# Revit family: LAMP_OCULT SUSPENDED PROFILE
name_source: partatom
category: Luminarias
revit_build: Autodesk Revit 2015 (Build: 20140606_1530(x64)
units: mm (PartAtom-declared; Revit-internal decimal feet)

## types (32) — shared parameters
Comentarios de tipo = Availability of changing profile version and height when placed in project.
Elevación por defecto = 1219 mm
Fabricante = LAMP
IEE = A+
Installation instructions = https://www.lamp.es
Insulation class = I
Last update = 25/07/2019
Luminaire type = Profile
Manufacturer URL = http://www.lamp.es
Manufacturer country = Spain
Manufacturer name = LAMP
Material suspension = Panel de metal
Model explanation = Availability of changing profile version and height when placed in project.
Product URL = https://www.lamp.es
Product datasheet = http://www.lamp.es
Protection rating = IP20

## per-type parameters (varying)
| type | Descripción | Dimensions | Finish | Length | Material perfil | Modelo | Product code | Weight |
| 500mm Surface  BLACK | OCULT SYS. ACC. SUR PROFILE 500 BK. | 500x53x96 | Matte black RAL 9011 | 500 mm  [stored 1.64042 ft] | LAMP_Aluminio Ocult Pendular NG | OSSUPR500B | OSSUPR500B | 0.84 kg |
| 500mm Surface  WHITE | OCULT SYS. ACC. SUR PROFILE 500 WH. | 500x53x96 | Matte white RAL 9010 | 500 mm  [stored 1.64042 ft] | LAMP_Aluminio Ocult Pendular BL | OSSUPR500W | OSSUPR500W | 0.84 kg |
| 600mm Surface  BLACK | OCULT SYS. ACC. SUR PROFILE 600 BK. | 600x53x96 | Matte black RAL 9011 | 600 mm | LAMP_Aluminio Ocult Pendular NG | OSSUPR600B | OSSUPR600B | 1.03 kg |
| 600mm Surface  WHITE | OCULT SYS. ACC. SUR PROFILE 600 WH. | 600x53x96 | Matte white RAL 9010 | 600 mm | LAMP_Aluminio Ocult Pendular BL | OSSUPR600W | OSSUPR600W | 1.03 kg |
| 700mm Surface  BLACK | OCULT SYS. ACC. SUR PROFILE 700 BK. | 700x53x96 | Matte black RAL 9011 | 700 mm  [stored 2.29659 ft] | LAMP_Aluminio Ocult Pendular NG | OSSUPR700B | OSSUPR700B | 1.35 kg |
| 700mm Surface  WHITE | OCULT SYS. ACC. SUR PROFILE 700 WH. | 700x53x96 | Matte white RAL 9010 | 700 mm  [stored 2.29659 ft] | LAMP_Aluminio Ocult Pendular BL | OSSUPR700W | OSSUPR700W | 1.35 kg |
| 800mm Surface  BLACK | OCULT SYS. ACC. SUR PROFILE 800 BK. | 800x53x96 | Matte black RAL 9011 | 800 mm  [stored 2.62467 ft] | LAMP_Aluminio Ocult Pendular NG | OSSUPR800B | OSSUPR800B | 1.53 kg |
| 800mm Surface  WHITE | OCULT SYS. ACC. SUR PROFILE 800 WH. | 800x53x96 | Matte white RAL 9010 | 800 mm  [stored 2.62467 ft] | LAMP_Aluminio Ocult Pendular BL | OSSUPR800W | OSSUPR800W | 1.53 kg |
| 900mm Surface  BLACK | OCULT SYS. ACC. SUR PROFILE 900 BK. | 900x53x96 | Matte black RAL 9011 | 900 mm  [stored 2.95276 ft] | LAMP_Aluminio Ocult Pendular NG | OSSUPR900B | OSSUPR900B | 1.72 kg |
| 900mm Surface  WHITE | OCULT SYS. ACC. SUR PROFILE 900 WH. | 900x53x96 | Matte white RAL 9010 | 900 mm  [stored 2.95276 ft] | LAMP_Aluminio Ocult Pendular BL | OSSUPR900W | OSSUPR900W | 1.72 kg |
| 1000mm Surface  BLACK | OCULT SYS. ACC. SUR PROFILE 1000 BK. | 1000x53x96 | Matte black RAL 9011 | 1000 mm  [stored 3.28084 ft] | LAMP_Aluminio Ocult Pendular NG | OSSUPR1000B | OSSUPR1000B | 1.91 kg |
| 1000mm Surface  WHITE | OCULT SYS. ACC. SUR PROFILE 1000 WH. | 1000x53x96 | Matte white RAL 9010 | 1000 mm  [stored 3.28084 ft] | LAMP_Aluminio Ocult Pendular BL | OSSUPR1000W | OSSUPR1000W | 1.91 kg |
| 1100mm Surface  BLACK | OCULT SYS. ACC. SUR PROFILE 1100 BK. | 1100x53x96 | Matte black RAL 9011 | 1100 mm | LAMP_Aluminio Ocult Pendular NG | OSSUPR1100B | OSSUPR1100B | 2.10 kg |
| 1100mm Surface  WHITE | OCULT SYS. ACC. SUR PROFILE 1100 WH. | 1100x53x96 | Matte white RAL 9010 | 1100 mm | LAMP_Aluminio Ocult Pendular BL | OSSUPR1100W | OSSUPR1100W | 2.10 kg |
| 1200mm Surface  BLACK | OCULT SYS. ACC. SUR PROFILE 1200 BK. | 1200x53x96 | Matte black RAL 9011 | 1200 mm | LAMP_Aluminio Ocult Pendular NG | OSSUPR1200B | OSSUPR1200B | 2.42 kg |
| 1200mm Surface  WHITE | OCULT SYS. ACC. SUR PROFILE 1200 WH. | 1200x53x96 | Matte white RAL 9010 | 1200 mm | LAMP_Aluminio Ocult Pendular BL | OSSUPR1200W | OSSUPR1200W | 2.42 kg |
| 1300mm Surface  BLACK | OCULT SYS. ACC. SUR PROFILE 1300 BK. | 1300x53x96 | Matte black RAL 9011 | 1300 mm  [stored 4.26509 ft] | LAMP_Aluminio Ocult Pendular NG | OSSUPR1300B | OSSUPR1300B | 2.61 kg |
| 1300mm Surface  WHITE | OCULT SYS. ACC. SUR PROFILE 1300 WH | 1300x53x96 | Matte white RAL 9010 | 1300 mm  [stored 4.26509 ft] | LAMP_Aluminio Ocult Pendular BL | OSSUPR1300W | OSSUPR1300W | 2.61 kg |
| 1400mm Surface  BLACK | OCULT SYS. ACC. SUR PROFILE 1400 BK. | 1400x53x96 | Matte black RAL 9011 | 1400 mm  [stored 4.59318 ft] | LAMP_Aluminio Ocult Pendular NG | OSSUPR1400B | OSSUPR1400B | 2.79 kg |
| 1400mm Surface  WHITE | OCULT SYS. ACC. SUR PROFILE 1400 WH. | 1400x53x96 | Matte white RAL 9010 | 1400 mm  [stored 4.59318 ft] | LAMP_Aluminio Ocult Pendular BL | OSSUPR1400W | OSSUPR1400W | 2.79 kg |
| 1500mm Surface  BLACK | OCULT SYS. ACC. SUR PROFILE 1500 BK. | 1500x53x96 | Matte black RAL 9011 | 1500 mm  [stored 4.92126 ft] | LAMP_Aluminio Ocult Pendular NG | OSSUPR1500B | OSSUPR1500B | 2.98 kg |
| 1500mm Surface  WHITE | OCULT SYS. ACC. SUR PROFILE 1500 WH. | 1500x53x96 | Matte white RAL 9010 | 1500 mm  [stored 4.92126 ft] | LAMP_Aluminio Ocult Pendular BL | OSSUPR1500W | OSSUPR1500W | 2.98 kg |
| 1600mm Surface  BLACK | OCULT SYS. ACC. SUR PROFILE 1600 BK. | 1600x53x96 | Matte black RAL 9011 | 1600 mm  [stored 5.24934 ft] | LAMP_Aluminio Ocult Pendular NG | OSSUPR1600B | OSSUPR1600B | 3.17 kg |
| 1600mm Surface  WHITE | OCULT SYS. ACC. SUR PROFILE 1600 WH. | 1600x53x96 | Matte white RAL 9010 | 1600 mm  [stored 5.24934 ft] | LAMP_Aluminio Ocult Pendular BL | OSSUPR1600W | OSSUPR1600W | 3.17 kg |
| 1700mm Surface  BLACK | OCULT SYS. ACC. SUR PROFILE 1700 BK. | 1700x53x96 | Matte black RAL 9011 | 1700 mm  [stored 5.57743 ft] | LAMP_Aluminio Ocult Pendular NG | OSSUPR1700B | OSSUPR1700B | 3.36 kg |
| 1700mm Surface  WHITE | OCULT SYS. ACC. SUR PROFILE 1700 WH. | 1700x53x96 | Matte white RAL 9010 | 1700 mm  [stored 5.57743 ft] | LAMP_Aluminio Ocult Pendular BL | OSSUPR1700W | OSSUPR1700W | 3.36 kg |
| 1800mm Surface  BLACK | OCULT SYS. ACC. SUR PROFILE 1800 BK. | 1800x53x96 | Matte black RAL 9011 | 1800 mm  [stored 5.90551 ft] | LAMP_Aluminio Ocult Pendular NG | OSSUPR1800B | OSSUPR1800B | 3.68 kg |
| 1800mm Surface  WHITE | OCULT SYS. ACC. SUR PROFILE 1800 WH. | 1800x53x96 | Matte white RAL 9010 | 1800 mm  [stored 5.90551 ft] | LAMP_Aluminio Ocult Pendular BL | OSSUPR1800W | OSSUPR1800W | 3.68 kg |
| 1900mm Surface  BLACK | OCULT SYS. ACC. SUR PROFILE 1900 BK. | 1900x53x96 | Matte black RAL 9011 | 1900 mm  [stored 6.2336 ft] | LAMP_Aluminio Ocult Pendular NG | OSSUPR1900B | OSSUPR1900B | 3.87 kg |
| 1900mm Surface  WHITE | OCULT SYS. ACC. SUR PROFILE 1900 WH. | 1900x53x96 | Matte white RAL 9010 | 1900 mm  [stored 6.2336 ft] | LAMP_Aluminio Ocult Pendular BL | OSSUPR1900W | OSSUPR1900W | 3.87 kg |
| 2000mm Surface  BLACK | OCULT SYS. ACC. SUR PROFILE 2000 BK. | 2000x53x96 | Matte black RAL 9011 | 2000 mm  [stored 6.56168 ft] | LAMP_Aluminio Ocult Pendular NG | OSSUPR2000B | OSSUPR2000B | 4.05 kg |
| 2000mm Surface  WHITE | OCULT SYS. ACC. SUR PROFILE 2000 WH. | 2000x53x96 | Matte white RAL 9010 | 2000 mm  [stored 6.56168 ft] | LAMP_Aluminio Ocult Pendular BL | OSSUPR2000W | OSSUPR2000W | 4.05 kg |

note: [stored X ft] marks values corroborated as IEEE doubles in the binary element streams (Revit-internal decimal feet)
